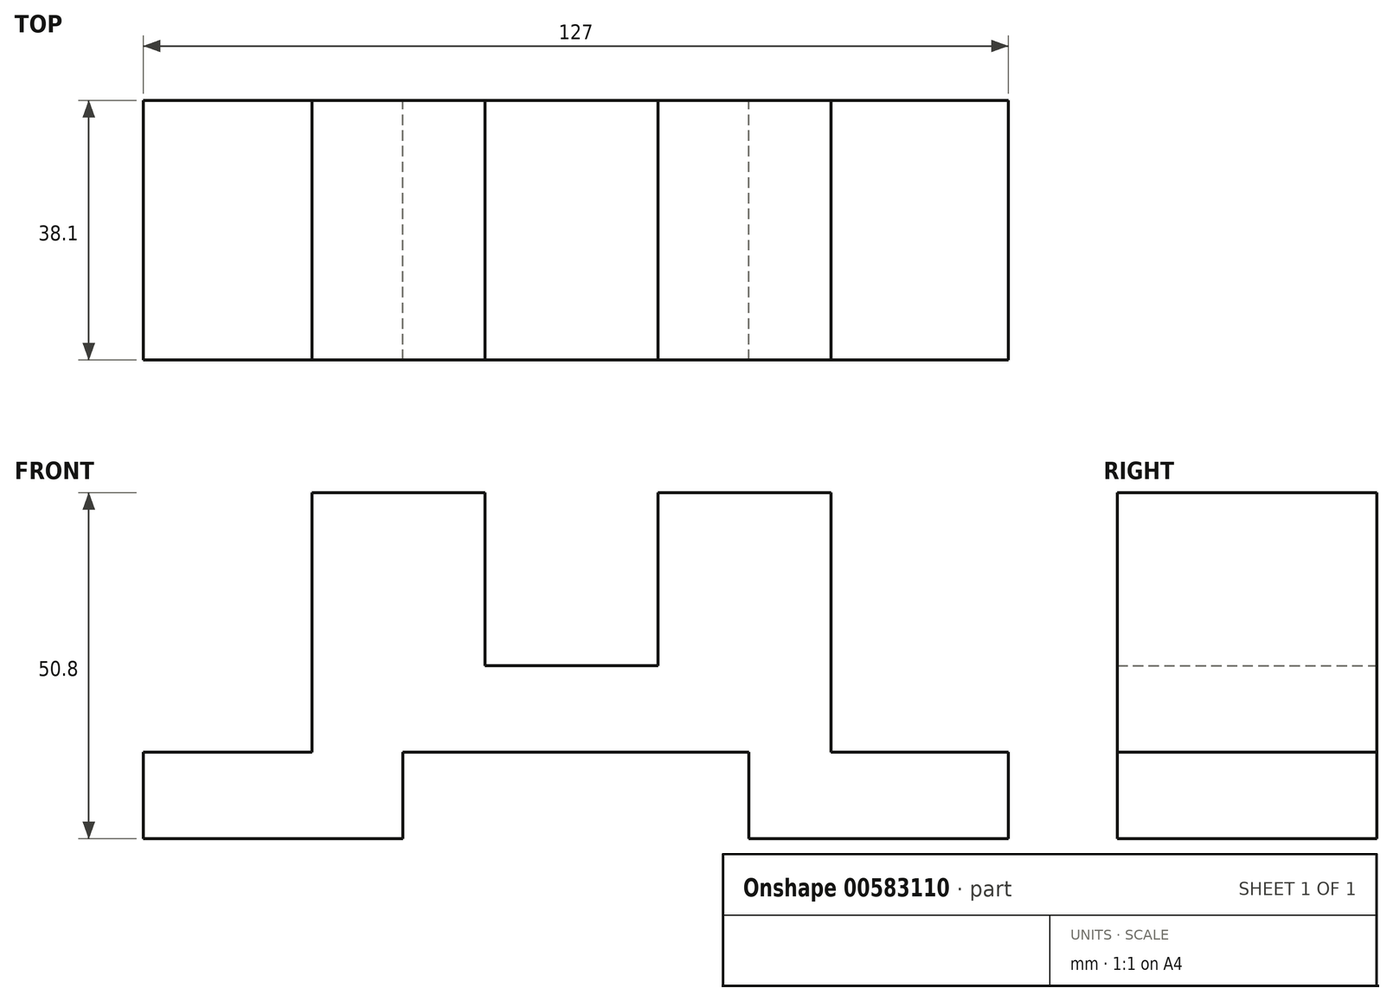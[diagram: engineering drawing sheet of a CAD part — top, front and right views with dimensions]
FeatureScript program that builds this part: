
annotation { "Feature Type Name" : "Feature", "Feature Type Description" : "" }
export const myFeature = defineFeature(function(context is Context, id is Id, definition is map)
    precondition{}
    {
        {
            var Q0;
            Q0=qCreatedBy(makeId("Front.planeOp"),FACE);
            var sketch = newSketch(context, id + "F0", { "sketchPlane" : qUnion([Q0])});
            skLineSegment(sketch, "E0", {"start": v(-36.66, -3.06) * mm, "end": v(-11.26, -3.06) * mm});
            skLineSegment(sketch, "E1", {"start": v(-11.26, -3.06) * mm, "end": v(-11.26, -28.46) * mm});
            skLineSegment(sketch, "E2", {"start": v(-11.26, -28.46) * mm, "end": v(14.14, -28.46) * mm});
            skLineSegment(sketch, "E3", {"start": v(14.14, -28.46) * mm, "end": v(14.14, -3.06) * mm});
            skLineSegment(sketch, "E4", {"start": v(14.14, -3.06) * mm, "end": v(39.54, -3.06) * mm});
            skLineSegment(sketch, "E5", {"start": v(39.54, -3.06) * mm, "end": v(39.54, -41.16) * mm});
            skLineSegment(sketch, "E6", {"start": v(39.54, -41.16) * mm, "end": v(65.6, -41.16) * mm});
            skLineSegment(sketch, "E7", {"start": v(65.6, -41.16) * mm, "end": v(65.6, -53.86) * mm});
            skLineSegment(sketch, "E8", {"start": v(65.6, -53.86) * mm, "end": v(27.5, -53.86) * mm});
            skLineSegment(sketch, "E9", {"start": v(27.5, -53.86) * mm, "end": v(27.5, -41.16) * mm});
            skLineSegment(sketch, "E10", {"start": v(27.5, -41.16) * mm, "end": v(-23.3, -41.16) * mm});
            skLineSegment(sketch, "E11", {"start": v(-23.3, -53.86) * mm, "end": v(-61.4, -53.86) * mm});
            skLineSegment(sketch, "E12", {"start": v(-61.4, -53.86) * mm, "end": v(-61.4, -41.16) * mm});
            skLineSegment(sketch, "E13", {"start": v(-61.4, -41.16) * mm, "end": v(-36.66, -41.16) * mm});
            skLineSegment(sketch, "E14", {"start": v(-36.66, -3.06) * mm, "end": v(-36.66, -41.16) * mm});
            skLineSegment(sketch, "E15", {"start": v(-23.3, -41.16) * mm, "end": v(-23.3, -53.86) * mm});
            skSolve(sketch);
        }
        {
            var Q0;
            Q0=makeQuery(id+"F0.imprint","IMPRINT",FACE,{"disambiguationData":[TD([[makeQuery(id+"F0.imprint","IMPRINT",EDGE,{"derivedFrom":sQuery(id+"F0.wireOp",EDGE,"E0")}),-1.0]])]});
            extrude(context, id + "F1", {"entities" : qUnion([Q0]), "depth" : 38.1 * mm, "offsetDistance" : 25.4 * mm});
        }
    });
